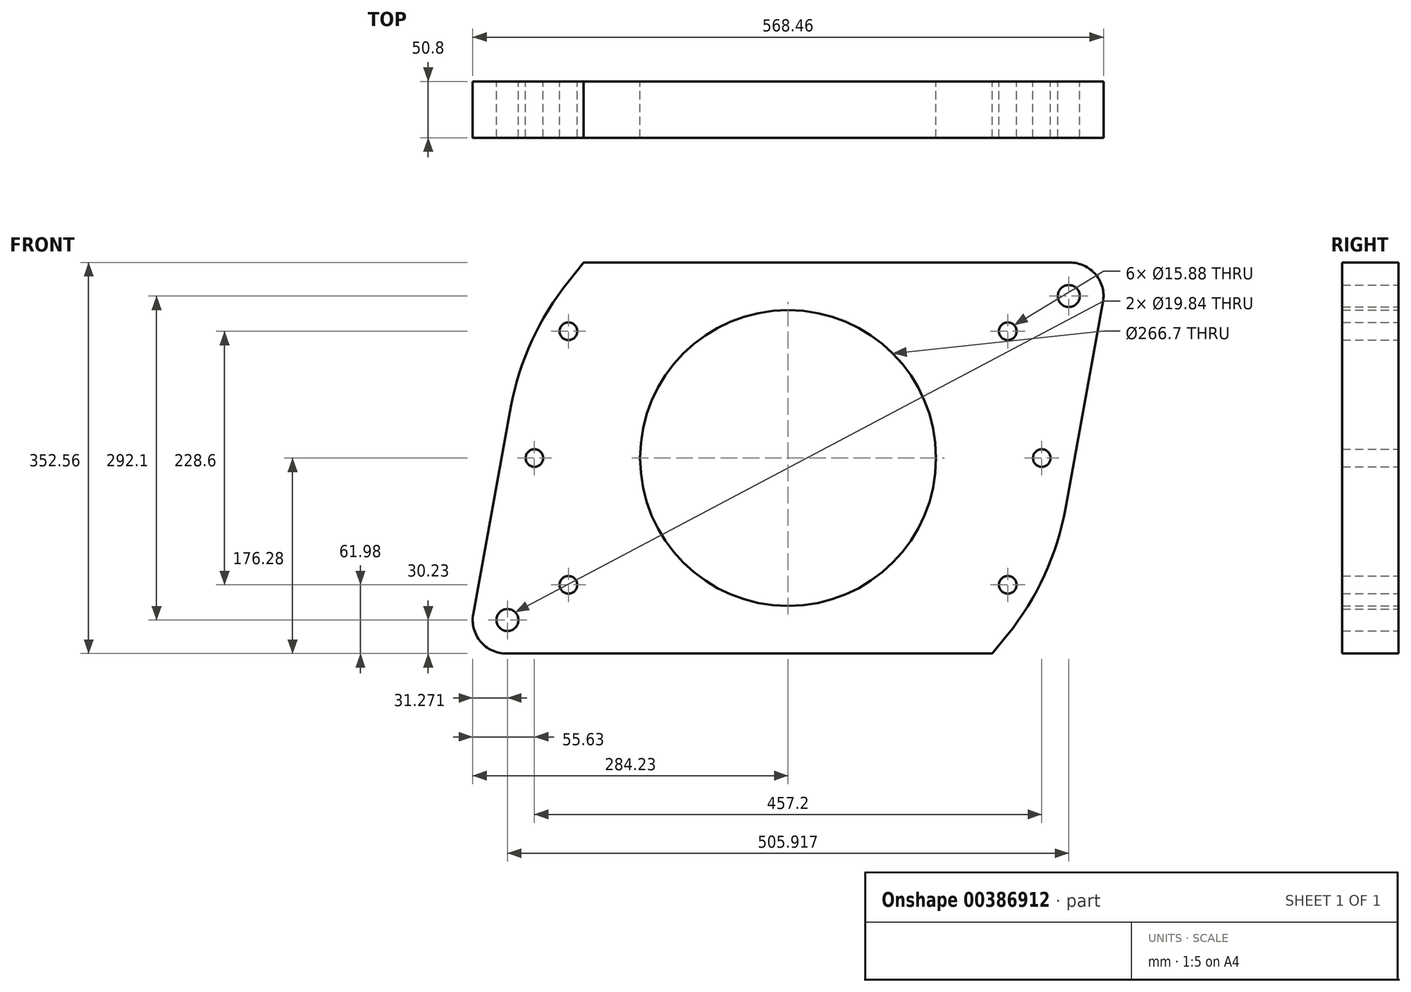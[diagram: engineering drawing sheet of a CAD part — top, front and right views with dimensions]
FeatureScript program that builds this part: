
annotation { "Feature Type Name" : "Feature", "Feature Type Description" : "" }
export const myFeature = defineFeature(function(context is Context, id is Id, definition is map)
    precondition{}
    {
        {
            var Q0;
            Q0=qCreatedBy(makeId("Front.planeOp"),FACE);
            var sketch = newSketch(context, id + "F0", { "sketchPlane" : qUnion([Q0])});
            skCircle(sketch, "E0", {"center": v(0, 0) * mm, "radius": 133.35 * mm});
            skArc(sketch, "E1", {"start": v(197.73, -159.43) * mm, "mid": v(230.96, -105.7) * mm, "end": v(249.9, -45.44) * mm});
            skLineSegment(sketch, "E2", {"start": v(0, -176.28) * mm, "end": v(184.15, -176.28) * mm});
            skLineSegment(sketch, "E3", {"start": v(0, -176.28) * mm, "end": v(-254, -176.28) * mm});
            skLineSegment(sketch, "E4", {"start": v(0, 176.28) * mm, "end": v(-184.15, 176.28) * mm});
            skLineSegment(sketch, "E5", {"start": v(0, 176.28) * mm, "end": v(254, 176.28) * mm});
            skLineSegment(sketch, "E6", {"start": v(-254, -146.05) * mm, "end": v(-207.81, -146.05) * mm, "construction": true});
            skLineSegment(sketch, "E7", {"start": v(232.71, 146.05) * mm, "end": v(254, 146.05) * mm, "construction": true});
            skArc(sketch, "E8", {"start": v(-283.74, -140.64) * mm, "mid": v(-277.2, -165.42) * mm, "end": v(-254, -176.28) * mm});
            skArc(sketch, "E9", {"start": v(283.74, 140.64) * mm, "mid": v(277.2, 165.42) * mm, "end": v(254, 176.28) * mm});
            skLineSegment(sketch, "E10", {"start": v(283.74, 140.64) * mm, "end": v(247.78, -57.1) * mm});
            skLineSegment(sketch, "E11", {"start": v(184.15, -176.28) * mm, "end": v(197.73, -159.43) * mm});
            skArc(sketch, "E12.trimOffspring", {"start": v(-197.73, 159.43) * mm, "mid": v(-230.96, 105.7) * mm, "end": v(-249.9, 45.44) * mm});
            skLineSegment(sketch, "E13", {"start": v(-283.74, -140.64) * mm, "end": v(-249.9, 45.44) * mm});
            skLineSegment(sketch, "E14", {"start": v(-184.15, 176.28) * mm, "end": v(-197.73, 159.43) * mm});
            skCircle(sketch, "E15", {"center": v(-197.97, 114.3) * mm, "radius": 7.94 * mm});
            skCircle(sketch, "E16", {"center": v(-228.6, 0) * mm, "radius": 7.94 * mm});
            skCircle(sketch, "E17", {"center": v(-197.97, -114.3) * mm, "radius": 7.94 * mm});
            skCircle(sketch, "E18", {"center": v(197.97, 114.3) * mm, "radius": 7.94 * mm});
            skCircle(sketch, "E19", {"center": v(228.6, 0) * mm, "radius": 7.94 * mm});
            skCircle(sketch, "E20", {"center": v(197.97, -114.3) * mm, "radius": 7.94 * mm});
            skCircle(sketch, "E21", {"center": v(252.96, 146.05) * mm, "radius": 9.92 * mm});
            skCircle(sketch, "E22", {"center": v(-252.96, -146.05) * mm, "radius": 9.92 * mm});
            skSolve(sketch);
        }
        {
            var Q0;
            Q0 = qSketchRegion(id + "F0", true);
            extrude(context, id + "F1", {"entities" : qUnion([Q0]), "depth" : 50.8 * mm});
        }
    });
